# Revit family: Practibox_S_cofrecito_empotrado_18_módulos_réf_137006_a_137179
name_source: partatom
category: Equipement électrique
revit_build: Autodesk Revit 2018 (Build: 20170223_1515(x64)
units: mm (PartAtom-declared; Revit-internal decimal feet)

## family parameters
Basée sur le plan de construction = Non
Configuration du panneau = Deux colonnes, circuits au sein
Cote de connecteur circulaire = Utiliser le diamètre
Couper avec des vides une fois chargée = Non
Numéro OmniClass = 23.80.30.11.17
Partagée = Non
Point de calcul de pièce = Non
Titre OmniClass = Distribution Boards and Control Panels
Toujours verticalement = Oui
Type d'élément = Tableau de raccordement

## types (32) — shared parameters
Condiciones Generales de Uso = https://export.legrand.com
Fabricant = "Legrand"
URL = www.legrand.com
anchura = 436 mm  [stored 1.43045 ft]

## per-type parameters (varying)
| type | 1R | 2R | 3R | 4R | Altura | Bornas N | Bornas T | Ina | profundidad | puerta B 1 r | puerta B 2 r | puerta B 3 r | puerta B 4 r | puerta T 1 r | puerta T 2 r | puerta T 3 r | puerta T 4 r | puerta blanca | puerta transparencia | tamaño |
| Practibox_S_cofrecito_empotrado_36_módulos_137027 | Non | Oui | Non | Non | 385 mm  [stored 1.26312 ft] |  |  | 90 A | 103 mm  [stored 0.337927 ft] | Non | Oui | Non | Non | Non | Non | Non | Non | Oui | Non | 2 fila |
| Practibox_S_cofrecito_empotrado_54_módulos_137028 | Non | Non | Oui | Non | 615 mm  [stored 2.01772 ft] |  |  | 90 A | 103 mm  [stored 0.337927 ft] | Non | Non | Oui | Non | Non | Non | Non | Non | Oui | Non | 3 fila |
| Practibox_S_cofrecito_empotrado_72_módulos_137029 | Non | Non | Non | Oui | 765 mm  [stored 2.50984 ft] |  |  | 90 A | 103 mm  [stored 0.337927 ft] | Non | Non | Non | Oui | Non | Non | Non | Non | Oui | Non | 4 fila |
| Practibox_S_cofrecito_empotrado_18_módulos_137026 | Oui | Non | Non | Non | 235 mm  [stored 0.770997 ft] |  |  | 63 A | 102 mm | Oui | Non | Non | Non | Non | Non | Non | Non | Oui | Non | 1 fila |
| Practibox_S_cofrecito_empotrado_18_módulos_137036 | Oui | Non | Non | Non | 235 mm  [stored 0.770997 ft] |  |  | 63 A | 102 mm | Non | Non | Non | Non | Oui | Non | Non | Non | Non | Oui | 1 fila |
| Practibox_S_cofrecito_empotrado_18_módulos_137176 | Oui | Non | Non | Non | 235 mm  [stored 0.770997 ft] | 17 salidas Icc 10kA | 17 salidas Icc 10kA | 63 A | 102 mm | Non | Non | Non | Non | Oui | Non | Non | Non | Non | Oui | 1 fila |
| Practibox_S_cofrecito_empotrado_18_módulos_137166 | Oui | Non | Non | Non | 235 mm  [stored 0.770997 ft] | 17 salidas Icc 10kA | 17 salidas Icc 10kA | 63 A | 102 mm | Oui | Non | Non | Non | Non | Non | Non | Non | Oui | Non | 1 fila |
| Practibox_S_cofrecito_empotrado_36_módulos_137037 | Non | Oui | Non | Non | 385 mm  [stored 1.26312 ft] |  |  | 90 A | 103 mm  [stored 0.337927 ft] | Non | Non | Non | Non | Non | Oui | Non | Non | Non | Oui | 2 fila |
| Practibox_S_cofrecito_empotrado_36_módulos_137177 | Non | Oui | Non | Non | 385 mm  [stored 1.26312 ft] | 27 salidas Icc 10kA | 27 salidas Icc 10kA | 90 A | 103 mm  [stored 0.337927 ft] | Non | Non | Non | Non | Non | Oui | Non | Non | Non | Oui | 2 fila |
| Practibox_S_cofrecito_empotrado_36_módulos_137167 | Non | Oui | Non | Non | 385 mm  [stored 1.26312 ft] | 27 salidas Icc 10kA | 27 salidas Icc 10kA | 90 A | 103 mm  [stored 0.337927 ft] | Non | Oui | Non | Non | Non | Non | Non | Non | Oui | Non | 2 fila |
| Practibox_S_cofrecito_empotrado_54_módulos_137038 | Non | Non | Oui | Non | 615 mm  [stored 2.01772 ft] |  |  | 90 A | 103 mm  [stored 0.337927 ft] | Non | Non | Non | Non | Non | Non | Oui | Non | Non | Oui | 3 fila |
| Practibox_S_cofrecito_empotrado_54_módulos_137168 | Non | Non | Oui | Non | 615 mm  [stored 2.01772 ft] | 27 salidas Icc 10kA | 27 salidas Icc 10kA | 90 A | 103 mm  [stored 0.337927 ft] | Non | Non | Oui | Non | Non | Non | Non | Non | Oui | Non | 3 fila |
| Practibox_S_cofrecito_empotrado_72_módulos_137039 | Non | Non | Non | Oui | 765 mm  [stored 2.50984 ft] |  |  | 90 A | 103 mm  [stored 0.337927 ft] | Non | Non | Non | Non | Non | Non | Non | Oui | Non | Oui | 4 fila |
| Practibox_S_cofrecito_empotrado_72_módulos_137169 | Non | Non | Non | Oui | 765 mm  [stored 2.50984 ft] | 27 salidas Icc 10kA | 27 salidas Icc 10kA | 90 A | 103 mm  [stored 0.337927 ft] | Non | Non | Non | Oui | Non | Non | Non | Non | Oui | Non | 4 fila |
| Practibox_S_cofrecito_empotrado_72_módulos_137179 | Non | Non | Non | Oui | 765 mm  [stored 2.50984 ft] | 27 salidas Icc 10kA | 27 salidas Icc 10kA | 90 A | 103 mm  [stored 0.337927 ft] | Non | Non | Non | Non | Non | Non | Non | Oui | Non | Oui | 4 fila |
| Practibox_S_cofrecito_empotrado_18_módulos_137006 | Oui | Non | Non | Non | 235 mm  [stored 0.770997 ft] |  |  | 63 A | 102 mm | Oui | Non | Non | Non | Non | Non | Non | Non | Oui | Non | 1 fila |
| Practibox_S_cofrecito_empotrado_18_módulos_137016 | Oui | Non | Non | Non | 235 mm  [stored 0.770997 ft] |  |  | 63 A | 102 mm | Non | Non | Non | Non | Oui | Non | Non | Non | Non | Oui | 1 fila |
| Practibox_S_cofrecito_empotrado_18_módulos_137156 | Oui | Non | Non | Non | 235 mm  [stored 0.770997 ft] | 17 salidas Icc 10kA | 17 salidas Icc 10kA | 63 A | 102 mm | Non | Non | Non | Non | Oui | Non | Non | Non | Non | Oui | 1 fila |
| Practibox_S_cofrecito_empotrado_18_módulos_137146 | Oui | Non | Non | Non | 235 mm  [stored 0.770997 ft] | 17 salidas Icc 10kA | 17 salidas Icc 10kA | 63 A | 102 mm | Oui | Non | Non | Non | Non | Non | Non | Non | Oui | Non | 1 fila |
| Practibox_S_cofrecito_empotrado_36_módulos_137007 | Non | Oui | Non | Non | 385 mm  [stored 1.26312 ft] |  |  | 90 A | 103 mm  [stored 0.337927 ft] | Non | Oui | Non | Non | Non | Non | Non | Non | Oui | Non | 2 fila |
| Practibox_S_cofrecito_empotrado_36_módulos_137017 | Non | Oui | Non | Non | 385 mm  [stored 1.26312 ft] |  |  | 90 A | 103 mm  [stored 0.337927 ft] | Non | Non | Non | Non | Non | Oui | Non | Non | Non | Oui | 2 fila |
| Practibox_S_cofrecito_empotrado_36_módulos_137157 | Non | Oui | Non | Non | 385 mm  [stored 1.26312 ft] | 27 salidas Icc 10kA | 27 salidas Icc 10kA | 90 A | 103 mm  [stored 0.337927 ft] | Non | Non | Non | Non | Non | Oui | Non | Non | Non | Oui | 2 fila |
| Practibox_S_cofrecito_empotrado_36_módulos_137147 | Non | Oui | Non | Non | 385 mm  [stored 1.26312 ft] | 27 salidas Icc 10kA | 27 salidas Icc 10kA | 90 A | 103 mm  [stored 0.337927 ft] | Non | Oui | Non | Non | Non | Non | Non | Non | Oui | Non | 2 fila |
| Practibox_S_cofrecito_empotrado_54_módulos_137008 | Non | Non | Oui | Non | 615 mm  [stored 2.01772 ft] |  |  | 90 A | 103 mm  [stored 0.337927 ft] | Non | Non | Oui | Non | Non | Non | Non | Non | Oui | Non | 3 fila |
| Practibox_S_cofrecito_empotrado_54_módulos_137018 | Non | Non | Oui | Non | 615 mm  [stored 2.01772 ft] |  |  | 90 A | 103 mm  [stored 0.337927 ft] | Non | Non | Non | Non | Non | Non | Oui | Non | Non | Oui | 3 fila |
| Practibox_S_cofrecito_empotrado_54_módulos_137158 | Non | Non | Oui | Non | 615 mm  [stored 2.01772 ft] | 27 salidas Icc 10kA | 27 salidas Icc 10kA | 90 A | 103 mm  [stored 0.337927 ft] | Non | Non | Non | Non | Non | Non | Oui | Non | Non | Oui | 3 fila |
| Practibox_S_cofrecito_empotrado_54_módulos_137148 | Non | Non | Oui | Non | 615 mm  [stored 2.01772 ft] | 27 salidas Icc 10kA | 27 salidas Icc 10kA | 90 A | 103 mm  [stored 0.337927 ft] | Non | Non | Oui | Non | Non | Non | Non | Non | Oui | Non | 3 fila |
| Practibox_S_cofrecito_empotrado_72_módulos_137009 | Non | Non | Non | Oui | 765 mm  [stored 2.50984 ft] |  |  | 90 A | 103 mm  [stored 0.337927 ft] | Non | Non | Non | Oui | Non | Non | Non | Non | Oui | Non | 4 fila |
| Practibox_S_cofrecito_empotrado_72_módulos_137019 | Non | Non | Non | Oui | 765 mm  [stored 2.50984 ft] |  |  | 90 A | 103 mm  [stored 0.337927 ft] | Non | Non | Non | Non | Non | Non | Non | Oui | Non | Oui | 4 fila |
| Practibox_S_cofrecito_empotrado_72_módulos_137159 | Non | Non | Non | Oui | 765 mm  [stored 2.50984 ft] | 27 salidas Icc 10kA | 27 salidas Icc 10kA | 90 A | 103 mm  [stored 0.337927 ft] | Non | Non | Non | Non | Non | Non | Non | Oui | Non | Oui | 4 fila |
| Practibox_S_cofrecito_empotrado_72_módulos_137149 | Non | Non | Non | Oui | 765 mm  [stored 2.50984 ft] | 27 salidas Icc 10kA | 27 salidas Icc 10kA | 90 A | 103 mm  [stored 0.337927 ft] | Non | Non | Non | Oui | Non | Non | Non | Non | Oui | Non | 4 fila |
| Practibox_S_cofrecito_empotrado_54_módulos_137178 | Non | Non | Oui | Non | 615 mm  [stored 2.01772 ft] | 27 salidas Icc 10kA | 27 salidas Icc 10kA | 90 A | 103 mm  [stored 0.337927 ft] | Non | Non | Non | Non | Non | Non | Oui | Non | Non | Oui | 3 fila |

note: column(s) folded — value = type name in every type: Description

note: [stored X ft] marks values corroborated as IEEE doubles in the binary element streams (Revit-internal decimal feet)
